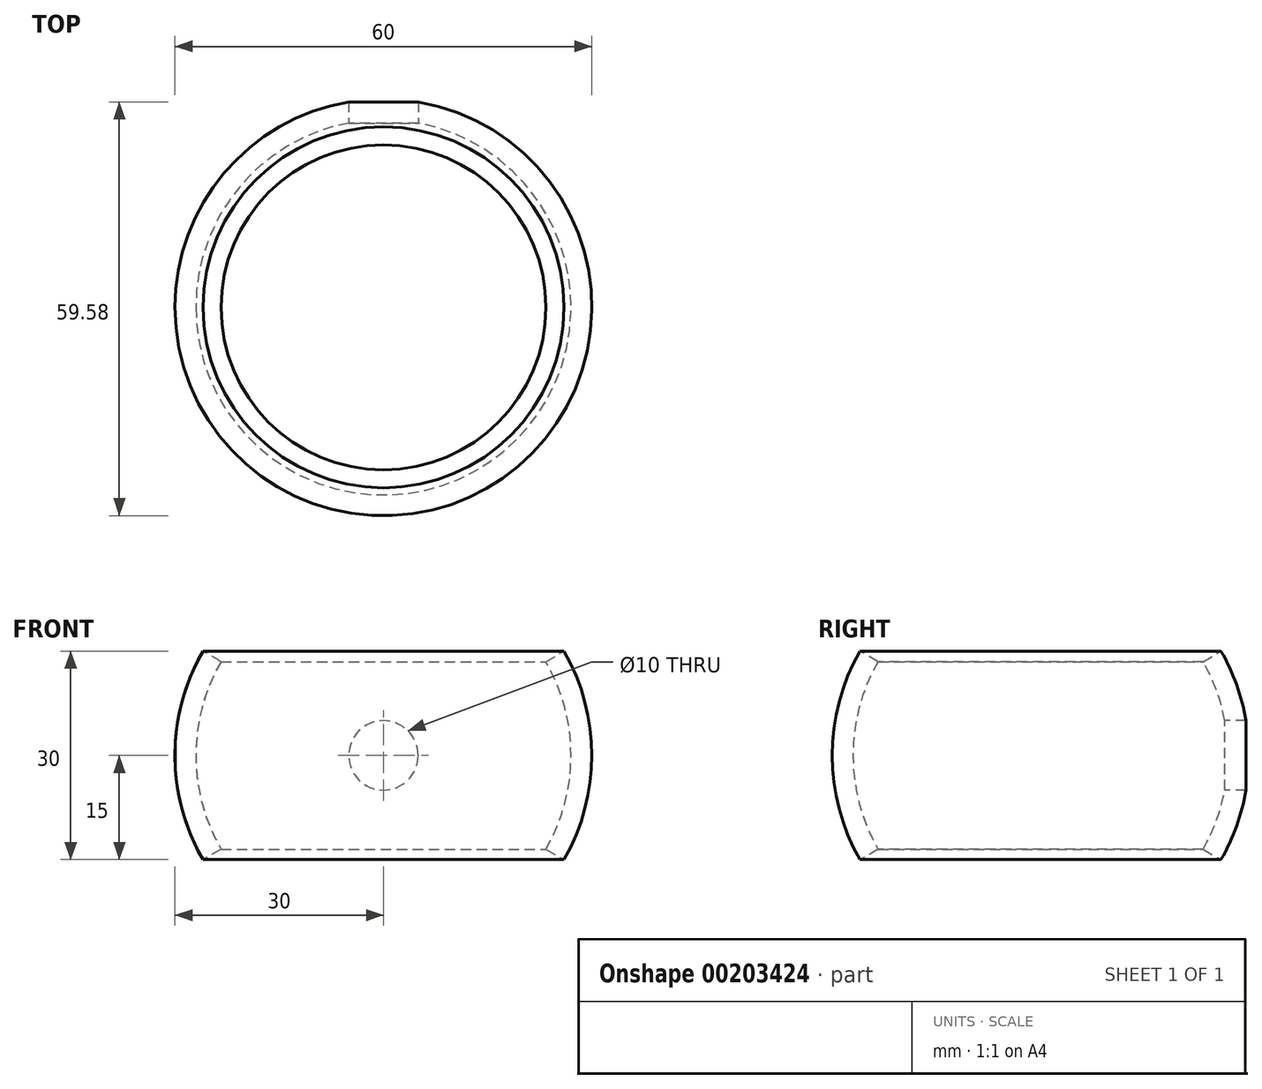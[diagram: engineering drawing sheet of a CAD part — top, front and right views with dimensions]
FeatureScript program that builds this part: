
annotation { "Feature Type Name" : "Feature", "Feature Type Description" : "" }
export const myFeature = defineFeature(function(context is Context, id is Id, definition is map)
    precondition{}
    {
        {
            var Q0;
            Q0=qCreatedBy(makeId("Front.planeOp"),FACE);
            var sketch = newSketch(context, id + "F0", { "sketchPlane" : qUnion([Q0])});
            skArc(sketch, "E0", {"start": v(25.98, -15) * mm, "mid": v(30, 0) * mm, "end": v(25.98, 15) * mm});
            skArc(sketch, "E1.0", {"start": v(23.38, -13.5) * mm, "mid": v(27, 0) * mm, "end": v(23.38, 13.5) * mm});
            skLineSegment(sketch, "E2", {"start": v(25.98, 15) * mm, "end": v(23.38, 13.5) * mm});
            skLineSegment(sketch, "E3", {"start": v(25.98, -15) * mm, "end": v(23.38, -13.5) * mm});
            skLineSegment(sketch, "E4", {"start": v(0, 0) * mm, "end": v(0, 9) * mm, "construction": true});
            skSolve(sketch);
        }
        {
            var Q0;
            Q0 = qSketchRegion(id + "F0", true);
            var Q1;
            Q1=sQuery(id+"F0.wireOp",EDGE,"E4");
            revolve(context, id + "F1", {"entities" : qUnion([Q0]), "axis" : qUnion([Q1]), "revolveType" : RevolveType.FULL});
        }
        {
            var Q0;
            Q0=qCreatedBy(makeId("Front.planeOp"),FACE);
            var sketch = newSketch(context, id + "F2", { "sketchPlane" : qUnion([Q0])});
            skCircle(sketch, "E5", {"center": v(0, 0) * mm, "radius": 5 * mm});
            skSolve(sketch);
        }
        {
            var Q0;
            Q0 = qSketchRegion(id + "F2", true);
            extrude(context, id + "F3", {"entities" : qUnion([Q0]), "operationType" : NewBodyOperationType.REMOVE, "endBound" : BoundingType.THROUGH_ALL, "oppositeDirection" : true, "depth" : 25 * mm});
        }
    });
